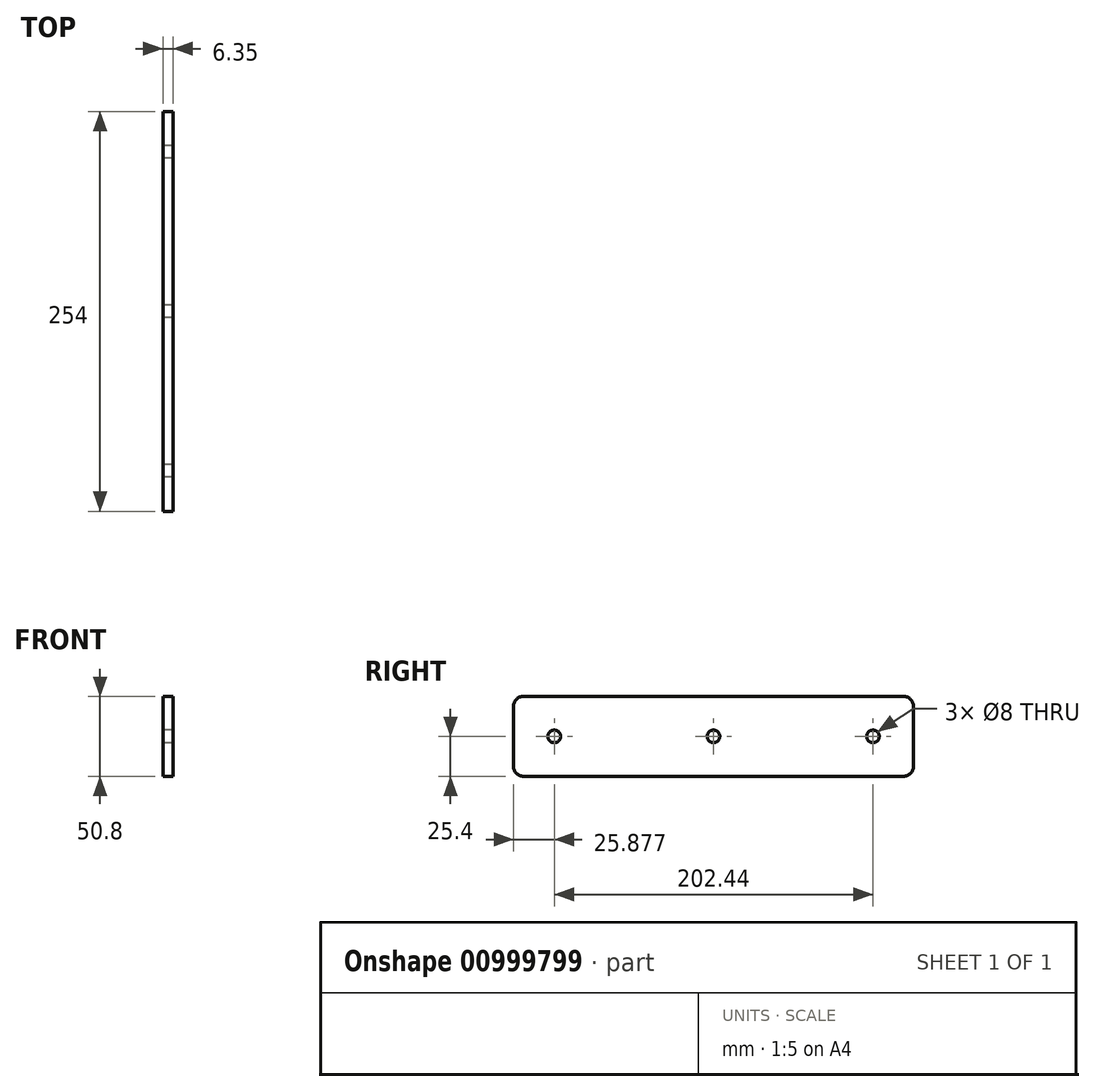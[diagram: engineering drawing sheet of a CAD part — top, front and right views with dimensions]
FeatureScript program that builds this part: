
annotation { "Feature Type Name" : "Feature", "Feature Type Description" : "" }
export const myFeature = defineFeature(function(context is Context, id is Id, definition is map)
    precondition{}
    {
        {
            var Q0;
            Q0=qCreatedBy(makeId("Right.planeOp"),FACE);
            var sketch = newSketch(context, id + "F0", { "sketchPlane" : qUnion([Q0])});
            skLineSegment(sketch, "E0.bottom", {"start": v(-120.65, 25.4) * mm, "end": v(120.65, 25.4) * mm});
            skLineSegment(sketch, "E0.top", {"start": v(-120.65, -25.4) * mm, "end": v(120.65, -25.4) * mm});
            skLineSegment(sketch, "E0.left", {"start": v(-127, 19.05) * mm, "end": v(-127, -19.05) * mm});
            skLineSegment(sketch, "E0.right", {"start": v(127, 19.05) * mm, "end": v(127, -19.05) * mm});
            skPoint(sketch, "E0.middle", {"position": v(0, 0) * mm});
            skPoint(sketch, "E1.visualSharp", {"position": v(-127, 25.4) * mm});
            skArc(sketch, "E1.filletArc", {"start": v(-120.65, 25.4) * mm, "mid": v(-125.14, 23.54) * mm, "end": v(-127, 19.05) * mm});
            skPoint(sketch, "E2.visualSharp", {"position": v(-127, -25.4) * mm});
            skArc(sketch, "E2.filletArc", {"start": v(-127, -19.05) * mm, "mid": v(-125.14, -23.54) * mm, "end": v(-120.65, -25.4) * mm});
            skPoint(sketch, "E3.visualSharp", {"position": v(127, 25.4) * mm});
            skArc(sketch, "E3.filletArc", {"start": v(127, 19.05) * mm, "mid": v(125.14, 23.54) * mm, "end": v(120.65, 25.4) * mm});
            skPoint(sketch, "E4.visualSharp", {"position": v(127, -25.4) * mm});
            skArc(sketch, "E4.filletArc", {"start": v(120.65, -25.4) * mm, "mid": v(125.14, -23.54) * mm, "end": v(127, -19.05) * mm});
            skCircle(sketch, "E5", {"center": v(0, 0) * mm, "radius": 4 * mm});
            skLineSegment(sketch, "E6", {"start": v(127, 0) * mm, "end": v(101.32, 0) * mm});
            skCircle(sketch, "E7", {"center": v(101.32, 0) * mm, "radius": 4 * mm});
            skLineSegment(sketch, "E8", {"start": v(-127, 0) * mm, "end": v(-101.12, 0) * mm});
            skCircle(sketch, "E9", {"center": v(-101.12, 0) * mm, "radius": 4 * mm});
            skSolve(sketch);
        }
        {
            var Q0;
            Q0=makeQuery(id+"F0.imprint","IMPRINT",FACE,{"disambiguationData":[TD([[makeQuery(id+"F0.imprint","IMPRINT",EDGE,{"derivedFrom":sQuery(id+"F0.wireOp",EDGE,"E0.bottom")}),-1.0]])]});
            extrude(context, id + "F1", {"entities" : qUnion([Q0]), "depth" : 6.35 * mm, "offsetDistance" : 25.4 * mm});
        }
    });
